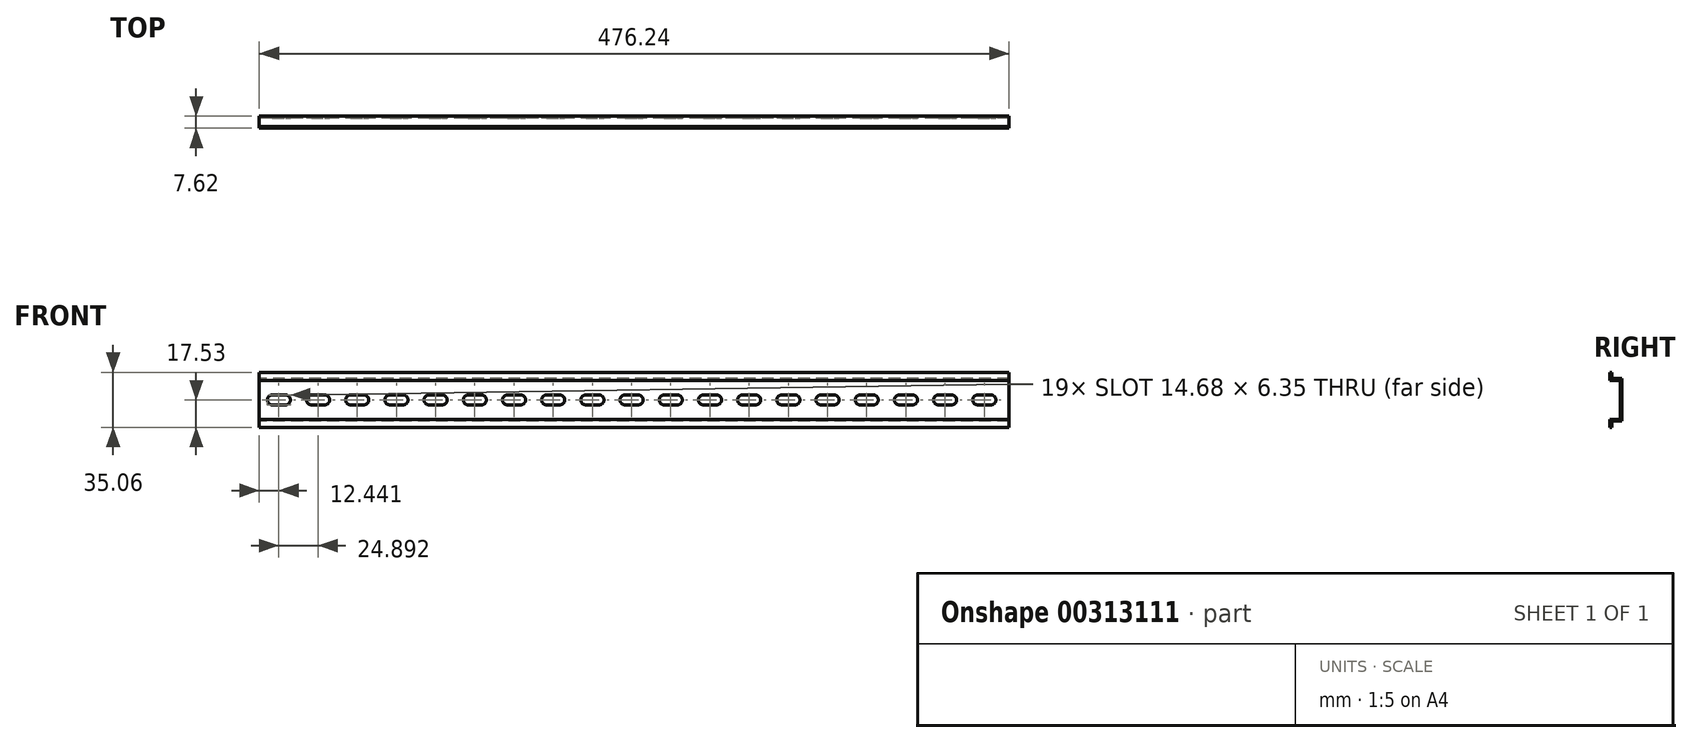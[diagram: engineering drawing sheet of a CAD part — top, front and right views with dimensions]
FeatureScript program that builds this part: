
annotation { "Feature Type Name" : "Feature", "Feature Type Description" : "" }
export const myFeature = defineFeature(function(context is Context, id is Id, definition is map)
    precondition{}
    {
        {
            var Q0;
            Q0=qCreatedBy(makeId("Right.planeOp"),FACE);
            var sketch = newSketch(context, id + "F0", { "sketchPlane" : qUnion([Q0])});
            skLineSegment(sketch, "E0", {"start": v(0, 17.53) * mm, "end": v(0, 12.45) * mm});
            skLineSegment(sketch, "E1", {"start": v(0, 12.45) * mm, "end": v(6.6, 12.45) * mm});
            skLineSegment(sketch, "E2", {"start": v(6.6, 12.45) * mm, "end": v(6.6, -12.45) * mm});
            skLineSegment(sketch, "E3", {"start": v(6.6, -12.45) * mm, "end": v(0, -12.45) * mm});
            skLineSegment(sketch, "E4", {"start": v(0, -12.45) * mm, "end": v(0, -17.53) * mm});
            skLineSegment(sketch, "E5", {"start": v(0, -17.53) * mm, "end": v(1.02, -17.53) * mm});
            skLineSegment(sketch, "E6", {"start": v(1.02, -17.53) * mm, "end": v(1.02, -13.46) * mm});
            skLineSegment(sketch, "E7", {"start": v(1.02, -13.46) * mm, "end": v(7.62, -13.46) * mm});
            skLineSegment(sketch, "E8", {"start": v(7.62, -13.46) * mm, "end": v(7.62, 13.46) * mm});
            skLineSegment(sketch, "E9", {"start": v(7.62, 13.46) * mm, "end": v(1.02, 13.46) * mm});
            skLineSegment(sketch, "E10", {"start": v(1.02, 13.46) * mm, "end": v(1.02, 17.53) * mm});
            skLineSegment(sketch, "E11", {"start": v(1.02, 17.53) * mm, "end": v(0, 17.53) * mm});
            skPoint(sketch, "E12", {"position": v(6.6, 0) * mm});
            skSolve(sketch);
        }
        {
            var Q0;
            Q0 = qSketchRegion(id + "F0", true);
            extrude(context, id + "F1", {"entities" : qUnion([Q0]), "endBound" : BoundingType.SYMMETRIC, "depth" : 476.25 * mm});
        }
        {
            var Q0;
            Q0=makeQuery(id+"F1.opExtrude","SWEPT_FACE",FACE,{"disambiguationData":[OSD([sQuery(id+"F0.wireOp",EDGE,"E2")])]});
            var sketch = newSketch(context, id + "F2", { "sketchPlane" : qUnion([Q0])});
            skArc(sketch, "E13", {"start": v(-229.85, -3.18) * mm, "mid": v(-233.02, 0) * mm, "end": v(-229.85, 3.18) * mm});
            skPoint(sketch, "E13.centerSnap0", {"position": v(-238.13, 0) * mm});
            skArc(sketch, "E14", {"start": v(-221.51, 3.18) * mm, "mid": v(-218.34, 0) * mm, "end": v(-221.51, -3.17) * mm});
            skLineSegment(sketch, "E15", {"start": v(-229.85, 3.17) * mm, "end": v(-221.51, 3.17) * mm});
            skLineSegment(sketch, "E16", {"start": v(-229.85, -3.17) * mm, "end": v(-221.51, -3.17) * mm});
            skPoint(sketch, "E17", {"position": v(-225.68, 3.18) * mm});
            skPoint(sketch, "E18", {"position": v(-225.68, -3.18) * mm});
            skLineSegment(sketch, "E19", {"start": v(-225.68, 3.18) * mm, "end": v(-225.68, -3.18) * mm, "construction": true});
            skPoint(sketch, "E20", {"position": v(-225.68, 0) * mm});
            skLineSegment(sketch, "E21.1.0.0", {"start": v(-204.95, 3.17) * mm, "end": v(-196.62, 3.17) * mm});
            skArc(sketch, "E21.1.0.1", {"start": v(-196.62, 3.18) * mm, "mid": v(-193.45, 0) * mm, "end": v(-196.62, -3.17) * mm});
            skLineSegment(sketch, "E21.1.0.2", {"start": v(-204.95, -3.17) * mm, "end": v(-196.62, -3.17) * mm});
            skArc(sketch, "E21.1.0.3", {"start": v(-204.95, -3.18) * mm, "mid": v(-208.13, 0) * mm, "end": v(-204.95, 3.18) * mm});
            skPoint(sketch, "E21.1.0.4", {"position": v(-200.79, 0) * mm});
            skPoint(sketch, "E21.1.0.5", {"position": v(-200.79, -3.18) * mm});
            skPoint(sketch, "E21.1.0.6", {"position": v(-200.79, 3.18) * mm});
            skPoint(sketch, "E21.1.0.7", {"position": v(-213.23, 0) * mm});
            skLineSegment(sketch, "E21.1.0.8", {"start": v(-200.79, 3.18) * mm, "end": v(-200.79, -3.18) * mm, "construction": true});
            skLineSegment(sketch, "E21.2.0.0", {"start": v(-180.06, 3.17) * mm, "end": v(-171.73, 3.17) * mm});
            skArc(sketch, "E21.2.0.1", {"start": v(-171.73, 3.18) * mm, "mid": v(-168.55, 0) * mm, "end": v(-171.73, -3.17) * mm});
            skLineSegment(sketch, "E21.2.0.2", {"start": v(-180.06, -3.17) * mm, "end": v(-171.73, -3.17) * mm});
            skArc(sketch, "E21.2.0.3", {"start": v(-180.06, -3.18) * mm, "mid": v(-183.24, 0) * mm, "end": v(-180.06, 3.18) * mm});
            skPoint(sketch, "E21.2.0.4", {"position": v(-175.9, 0) * mm});
            skPoint(sketch, "E21.2.0.5", {"position": v(-175.9, -3.18) * mm});
            skPoint(sketch, "E21.2.0.6", {"position": v(-175.9, 3.18) * mm});
            skPoint(sketch, "E21.2.0.7", {"position": v(-188.34, 0) * mm});
            skLineSegment(sketch, "E21.2.0.8", {"start": v(-175.9, 3.18) * mm, "end": v(-175.9, -3.18) * mm, "construction": true});
            skLineSegment(sketch, "E21.3.0.0", {"start": v(-155.17, 3.17) * mm, "end": v(-146.84, 3.17) * mm});
            skArc(sketch, "E21.3.0.1", {"start": v(-146.84, 3.18) * mm, "mid": v(-143.66, 0) * mm, "end": v(-146.84, -3.17) * mm});
            skLineSegment(sketch, "E21.3.0.2", {"start": v(-155.17, -3.17) * mm, "end": v(-146.84, -3.17) * mm});
            skArc(sketch, "E21.3.0.3", {"start": v(-155.17, -3.18) * mm, "mid": v(-158.34, 0) * mm, "end": v(-155.17, 3.18) * mm});
            skPoint(sketch, "E21.3.0.4", {"position": v(-151, 0) * mm});
            skPoint(sketch, "E21.3.0.5", {"position": v(-151, -3.18) * mm});
            skPoint(sketch, "E21.3.0.6", {"position": v(-151, 3.18) * mm});
            skPoint(sketch, "E21.3.0.7", {"position": v(-163.45, 0) * mm});
            skLineSegment(sketch, "E21.3.0.8", {"start": v(-151, 3.18) * mm, "end": v(-151, -3.18) * mm, "construction": true});
            skLineSegment(sketch, "E21.4.0.0", {"start": v(-130.28, 3.17) * mm, "end": v(-121.94, 3.17) * mm});
            skArc(sketch, "E21.4.0.1", {"start": v(-121.94, 3.18) * mm, "mid": v(-118.77, 0) * mm, "end": v(-121.94, -3.17) * mm});
            skLineSegment(sketch, "E21.4.0.2", {"start": v(-130.28, -3.17) * mm, "end": v(-121.94, -3.17) * mm});
            skArc(sketch, "E21.4.0.3", {"start": v(-130.28, -3.18) * mm, "mid": v(-133.45, 0) * mm, "end": v(-130.28, 3.18) * mm});
            skPoint(sketch, "E21.4.0.4", {"position": v(-126.11, 0) * mm});
            skPoint(sketch, "E21.4.0.5", {"position": v(-126.11, -3.18) * mm});
            skPoint(sketch, "E21.4.0.6", {"position": v(-126.11, 3.18) * mm});
            skPoint(sketch, "E21.4.0.7", {"position": v(-138.56, 0) * mm});
            skLineSegment(sketch, "E21.4.0.8", {"start": v(-126.11, 3.18) * mm, "end": v(-126.11, -3.18) * mm, "construction": true});
            skLineSegment(sketch, "E21.5.0.0", {"start": v(-105.39, 3.17) * mm, "end": v(-97.05, 3.17) * mm});
            skArc(sketch, "E21.5.0.1", {"start": v(-97.05, 3.18) * mm, "mid": v(-93.88, 0) * mm, "end": v(-97.05, -3.17) * mm});
            skLineSegment(sketch, "E21.5.0.2", {"start": v(-105.39, -3.17) * mm, "end": v(-97.05, -3.17) * mm});
            skArc(sketch, "E21.5.0.3", {"start": v(-105.39, -3.18) * mm, "mid": v(-108.56, 0) * mm, "end": v(-105.39, 3.18) * mm});
            skPoint(sketch, "E21.5.0.4", {"position": v(-101.22, 0) * mm});
            skPoint(sketch, "E21.5.0.5", {"position": v(-101.22, -3.18) * mm});
            skPoint(sketch, "E21.5.0.6", {"position": v(-101.22, 3.18) * mm});
            skPoint(sketch, "E21.5.0.7", {"position": v(-113.67, 0) * mm});
            skLineSegment(sketch, "E21.5.0.8", {"start": v(-101.22, 3.18) * mm, "end": v(-101.22, -3.18) * mm, "construction": true});
            skLineSegment(sketch, "E21.6.0.0", {"start": v(-80.5, 3.17) * mm, "end": v(-72.16, 3.17) * mm});
            skArc(sketch, "E21.6.0.1", {"start": v(-72.16, 3.18) * mm, "mid": v(-68.99, 0) * mm, "end": v(-72.16, -3.17) * mm});
            skLineSegment(sketch, "E21.6.0.2", {"start": v(-80.5, -3.17) * mm, "end": v(-72.16, -3.17) * mm});
            skArc(sketch, "E21.6.0.3", {"start": v(-80.5, -3.18) * mm, "mid": v(-83.67, 0) * mm, "end": v(-80.5, 3.18) * mm});
            skPoint(sketch, "E21.6.0.4", {"position": v(-76.33, 0) * mm});
            skPoint(sketch, "E21.6.0.5", {"position": v(-76.33, -3.18) * mm});
            skPoint(sketch, "E21.6.0.6", {"position": v(-76.33, 3.18) * mm});
            skPoint(sketch, "E21.6.0.7", {"position": v(-88.77, 0) * mm});
            skLineSegment(sketch, "E21.6.0.8", {"start": v(-76.33, 3.18) * mm, "end": v(-76.33, -3.18) * mm, "construction": true});
            skLineSegment(sketch, "E21.7.0.0", {"start": v(-55.6, 3.17) * mm, "end": v(-47.27, 3.17) * mm});
            skArc(sketch, "E21.7.0.1", {"start": v(-47.27, 3.18) * mm, "mid": v(-44.1, 0) * mm, "end": v(-47.27, -3.17) * mm});
            skLineSegment(sketch, "E21.7.0.2", {"start": v(-55.6, -3.17) * mm, "end": v(-47.27, -3.17) * mm});
            skArc(sketch, "E21.7.0.3", {"start": v(-55.6, -3.18) * mm, "mid": v(-58.78, 0) * mm, "end": v(-55.6, 3.18) * mm});
            skPoint(sketch, "E21.7.0.4", {"position": v(-51.44, 0) * mm});
            skPoint(sketch, "E21.7.0.5", {"position": v(-51.43, -3.18) * mm});
            skPoint(sketch, "E21.7.0.6", {"position": v(-51.44, 3.18) * mm});
            skPoint(sketch, "E21.7.0.7", {"position": v(-63.88, 0) * mm});
            skLineSegment(sketch, "E21.7.0.8", {"start": v(-51.44, 3.18) * mm, "end": v(-51.43, -3.18) * mm, "construction": true});
            skLineSegment(sketch, "E21.8.0.0", {"start": v(-30.7, 3.17) * mm, "end": v(-22.38, 3.17) * mm});
            skArc(sketch, "E21.8.0.1", {"start": v(-22.38, 3.18) * mm, "mid": v(-19.2, 0) * mm, "end": v(-22.38, -3.17) * mm});
            skLineSegment(sketch, "E21.8.0.2", {"start": v(-30.7, -3.17) * mm, "end": v(-22.38, -3.17) * mm});
            skArc(sketch, "E21.8.0.3", {"start": v(-30.7, -3.18) * mm, "mid": v(-33.88, 0) * mm, "end": v(-30.7, 3.18) * mm});
            skPoint(sketch, "E21.8.0.4", {"position": v(-26.54, 0) * mm});
            skPoint(sketch, "E21.8.0.5", {"position": v(-26.54, -3.18) * mm});
            skPoint(sketch, "E21.8.0.6", {"position": v(-26.54, 3.18) * mm});
            skPoint(sketch, "E21.8.0.7", {"position": v(-38.99, 0) * mm});
            skLineSegment(sketch, "E21.8.0.8", {"start": v(-26.54, 3.18) * mm, "end": v(-26.54, -3.18) * mm, "construction": true});
            skLineSegment(sketch, "E21.9.0.0", {"start": v(-5.82, 3.17) * mm, "end": v(2.52, 3.17) * mm});
            skArc(sketch, "E21.9.0.1", {"start": v(2.52, 3.18) * mm, "mid": v(5.7, 0) * mm, "end": v(2.52, -3.17) * mm});
            skLineSegment(sketch, "E21.9.0.2", {"start": v(-5.82, -3.17) * mm, "end": v(2.52, -3.17) * mm});
            skArc(sketch, "E21.9.0.3", {"start": v(-5.82, -3.18) * mm, "mid": v(-9, 0) * mm, "end": v(-5.82, 3.18) * mm});
            skPoint(sketch, "E21.9.0.4", {"position": v(-1.65, 0) * mm});
            skPoint(sketch, "E21.9.0.5", {"position": v(-1.65, -3.18) * mm});
            skPoint(sketch, "E21.9.0.6", {"position": v(-1.65, 3.18) * mm});
            skPoint(sketch, "E21.9.0.7", {"position": v(-14.1, 0) * mm});
            skLineSegment(sketch, "E21.9.0.8", {"start": v(-1.65, 3.18) * mm, "end": v(-1.65, -3.18) * mm, "construction": true});
            skLineSegment(sketch, "E21.10.0.0", {"start": v(19.07, 3.17) * mm, "end": v(27.4, 3.17) * mm});
            skArc(sketch, "E21.10.0.1", {"start": v(27.4, 3.18) * mm, "mid": v(30.58, 0) * mm, "end": v(27.4, -3.17) * mm});
            skLineSegment(sketch, "E21.10.0.2", {"start": v(19.07, -3.17) * mm, "end": v(27.4, -3.17) * mm});
            skArc(sketch, "E21.10.0.3", {"start": v(19.07, -3.18) * mm, "mid": v(15.9, 0) * mm, "end": v(19.07, 3.18) * mm});
            skPoint(sketch, "E21.10.0.4", {"position": v(23.24, 0) * mm});
            skPoint(sketch, "E21.10.0.5", {"position": v(23.24, -3.18) * mm});
            skPoint(sketch, "E21.10.0.6", {"position": v(23.24, 3.18) * mm});
            skPoint(sketch, "E21.10.0.7", {"position": v(10.8, 0) * mm});
            skLineSegment(sketch, "E21.10.0.8", {"start": v(23.24, 3.18) * mm, "end": v(23.24, -3.18) * mm, "construction": true});
            skLineSegment(sketch, "E21.11.0.0", {"start": v(43.97, 3.17) * mm, "end": v(52.3, 3.17) * mm});
            skArc(sketch, "E21.11.0.1", {"start": v(52.3, 3.18) * mm, "mid": v(55.47, 0) * mm, "end": v(52.3, -3.17) * mm});
            skLineSegment(sketch, "E21.11.0.2", {"start": v(43.97, -3.17) * mm, "end": v(52.3, -3.17) * mm});
            skArc(sketch, "E21.11.0.3", {"start": v(43.97, -3.18) * mm, "mid": v(40.8, 0) * mm, "end": v(43.97, 3.18) * mm});
            skPoint(sketch, "E21.11.0.4", {"position": v(48.13, 0) * mm});
            skPoint(sketch, "E21.11.0.5", {"position": v(48.13, -3.18) * mm});
            skPoint(sketch, "E21.11.0.6", {"position": v(48.13, 3.18) * mm});
            skPoint(sketch, "E21.11.0.7", {"position": v(35.69, 0) * mm});
            skLineSegment(sketch, "E21.11.0.8", {"start": v(48.13, 3.18) * mm, "end": v(48.13, -3.18) * mm, "construction": true});
            skLineSegment(sketch, "E21.12.0.0", {"start": v(68.86, 3.17) * mm, "end": v(77.2, 3.17) * mm});
            skArc(sketch, "E21.12.0.1", {"start": v(77.2, 3.18) * mm, "mid": v(80.37, 0) * mm, "end": v(77.2, -3.17) * mm});
            skLineSegment(sketch, "E21.12.0.2", {"start": v(68.86, -3.17) * mm, "end": v(77.2, -3.17) * mm});
            skArc(sketch, "E21.12.0.3", {"start": v(68.86, -3.18) * mm, "mid": v(65.68, 0) * mm, "end": v(68.86, 3.18) * mm});
            skPoint(sketch, "E21.12.0.4", {"position": v(73.02, 0) * mm});
            skPoint(sketch, "E21.12.0.5", {"position": v(73.03, -3.18) * mm});
            skPoint(sketch, "E21.12.0.6", {"position": v(73.02, 3.18) * mm});
            skPoint(sketch, "E21.12.0.7", {"position": v(60.58, 0) * mm});
            skLineSegment(sketch, "E21.12.0.8", {"start": v(73.02, 3.18) * mm, "end": v(73.03, -3.18) * mm, "construction": true});
            skLineSegment(sketch, "E21.13.0.0", {"start": v(93.75, 3.17) * mm, "end": v(102.08, 3.17) * mm});
            skArc(sketch, "E21.13.0.1", {"start": v(102.08, 3.18) * mm, "mid": v(105.26, 0) * mm, "end": v(102.08, -3.17) * mm});
            skLineSegment(sketch, "E21.13.0.2", {"start": v(93.75, -3.17) * mm, "end": v(102.08, -3.17) * mm});
            skArc(sketch, "E21.13.0.3", {"start": v(93.75, -3.18) * mm, "mid": v(90.58, 0) * mm, "end": v(93.75, 3.18) * mm});
            skPoint(sketch, "E21.13.0.4", {"position": v(97.92, 0) * mm});
            skPoint(sketch, "E21.13.0.5", {"position": v(97.92, -3.18) * mm});
            skPoint(sketch, "E21.13.0.6", {"position": v(97.92, 3.18) * mm});
            skPoint(sketch, "E21.13.0.7", {"position": v(85.47, 0) * mm});
            skLineSegment(sketch, "E21.13.0.8", {"start": v(97.92, 3.18) * mm, "end": v(97.92, -3.18) * mm, "construction": true});
            skLineSegment(sketch, "E21.direction1", {"start": v(-238.13, 0) * mm, "end": v(-213.23, 0) * mm, "construction": true});
            skLineSegment(sketch, "E22.0.14.0", {"start": v(118.64, 3.17) * mm, "end": v(126.98, 3.17) * mm});
            skArc(sketch, "E22.3.14.0", {"start": v(126.98, 3.18) * mm, "mid": v(130.15, 0) * mm, "end": v(126.98, -3.17) * mm});
            skLineSegment(sketch, "E22.7.14.0", {"start": v(118.64, -3.17) * mm, "end": v(126.98, -3.17) * mm});
            skArc(sketch, "E22.10.14.0", {"start": v(118.64, -3.18) * mm, "mid": v(115.47, 0) * mm, "end": v(118.64, 3.18) * mm});
            skPoint(sketch, "E22.14.14.0", {"position": v(122.8, 0) * mm});
            skPoint(sketch, "E22.15.14.0", {"position": v(122.8, -3.18) * mm});
            skPoint(sketch, "E22.16.14.0", {"position": v(122.8, 3.18) * mm});
            skPoint(sketch, "E22.17.14.0", {"position": v(110.36, 0) * mm});
            skLineSegment(sketch, "E22.18.14.0", {"start": v(122.8, 3.18) * mm, "end": v(122.8, -3.18) * mm, "construction": true});
            skLineSegment(sketch, "E23.0.15.0", {"start": v(143.53, 3.17) * mm, "end": v(151.87, 3.17) * mm});
            skArc(sketch, "E23.3.15.0", {"start": v(151.87, 3.18) * mm, "mid": v(155.04, 0) * mm, "end": v(151.87, -3.17) * mm});
            skLineSegment(sketch, "E23.7.15.0", {"start": v(143.53, -3.17) * mm, "end": v(151.87, -3.17) * mm});
            skArc(sketch, "E23.10.15.0", {"start": v(143.53, -3.18) * mm, "mid": v(140.36, 0) * mm, "end": v(143.53, 3.18) * mm});
            skPoint(sketch, "E23.14.15.0", {"position": v(147.7, 0) * mm});
            skPoint(sketch, "E23.15.15.0", {"position": v(147.7, -3.18) * mm});
            skPoint(sketch, "E23.16.15.0", {"position": v(147.7, 3.18) * mm});
            skPoint(sketch, "E23.17.15.0", {"position": v(135.25, 0) * mm});
            skLineSegment(sketch, "E23.18.15.0", {"start": v(147.7, 3.18) * mm, "end": v(147.7, -3.18) * mm, "construction": true});
            skLineSegment(sketch, "E24.0.16.0", {"start": v(168.43, 3.17) * mm, "end": v(176.76, 3.17) * mm});
            skArc(sketch, "E24.3.16.0", {"start": v(176.76, 3.18) * mm, "mid": v(179.93, 0) * mm, "end": v(176.76, -3.17) * mm});
            skLineSegment(sketch, "E24.7.16.0", {"start": v(168.43, -3.17) * mm, "end": v(176.76, -3.17) * mm});
            skArc(sketch, "E24.10.16.0", {"start": v(168.43, -3.18) * mm, "mid": v(165.25, 0) * mm, "end": v(168.43, 3.18) * mm});
            skPoint(sketch, "E24.14.16.0", {"position": v(172.6, 0) * mm});
            skPoint(sketch, "E24.15.16.0", {"position": v(172.6, -3.18) * mm});
            skPoint(sketch, "E24.16.16.0", {"position": v(172.6, 3.18) * mm});
            skPoint(sketch, "E24.17.16.0", {"position": v(160.15, 0) * mm});
            skLineSegment(sketch, "E24.18.16.0", {"start": v(172.6, 3.18) * mm, "end": v(172.6, -3.18) * mm, "construction": true});
            skLineSegment(sketch, "E24.0.17.0", {"start": v(193.32, 3.17) * mm, "end": v(201.65, 3.17) * mm});
            skArc(sketch, "E24.3.17.0", {"start": v(201.65, 3.18) * mm, "mid": v(204.83, 0) * mm, "end": v(201.65, -3.17) * mm});
            skLineSegment(sketch, "E24.7.17.0", {"start": v(193.32, -3.17) * mm, "end": v(201.65, -3.17) * mm});
            skArc(sketch, "E24.10.17.0", {"start": v(193.32, -3.18) * mm, "mid": v(190.14, 0) * mm, "end": v(193.32, 3.18) * mm});
            skPoint(sketch, "E24.14.17.0", {"position": v(197.48, 0) * mm});
            skPoint(sketch, "E24.15.17.0", {"position": v(197.49, -3.18) * mm});
            skPoint(sketch, "E24.16.17.0", {"position": v(197.48, 3.18) * mm});
            skPoint(sketch, "E24.17.17.0", {"position": v(185.04, 0) * mm});
            skLineSegment(sketch, "E24.18.17.0", {"start": v(197.48, 3.18) * mm, "end": v(197.49, -3.18) * mm, "construction": true});
            skLineSegment(sketch, "E24.0.18.0", {"start": v(218.21, 3.17) * mm, "end": v(226.54, 3.17) * mm});
            skArc(sketch, "E24.3.18.0", {"start": v(226.54, 3.18) * mm, "mid": v(229.72, 0) * mm, "end": v(226.54, -3.17) * mm});
            skLineSegment(sketch, "E24.7.18.0", {"start": v(218.21, -3.17) * mm, "end": v(226.54, -3.17) * mm});
            skArc(sketch, "E24.10.18.0", {"start": v(218.21, -3.18) * mm, "mid": v(215.04, 0) * mm, "end": v(218.21, 3.18) * mm});
            skPoint(sketch, "E24.14.18.0", {"position": v(222.38, 0) * mm});
            skPoint(sketch, "E24.15.18.0", {"position": v(222.38, -3.18) * mm});
            skPoint(sketch, "E24.16.18.0", {"position": v(222.38, 3.18) * mm});
            skPoint(sketch, "E24.17.18.0", {"position": v(209.93, 0) * mm});
            skLineSegment(sketch, "E24.18.18.0", {"start": v(222.38, 3.18) * mm, "end": v(222.38, -3.18) * mm, "construction": true});
            skLineSegment(sketch, "E24.0.19.0", {"start": v(243.1, 3.17) * mm, "end": v(251.44, 3.17) * mm});
            skArc(sketch, "E24.3.19.0", {"start": v(251.44, 3.18) * mm, "mid": v(254.61, 0) * mm, "end": v(251.44, -3.17) * mm});
            skLineSegment(sketch, "E24.7.19.0", {"start": v(243.1, -3.17) * mm, "end": v(251.44, -3.17) * mm});
            skArc(sketch, "E24.10.19.0", {"start": v(243.1, -3.18) * mm, "mid": v(239.93, 0) * mm, "end": v(243.1, 3.18) * mm});
            skPoint(sketch, "E24.14.19.0", {"position": v(247.27, 0) * mm});
            skPoint(sketch, "E24.15.19.0", {"position": v(247.27, -3.18) * mm});
            skPoint(sketch, "E24.16.19.0", {"position": v(247.27, 3.18) * mm});
            skPoint(sketch, "E24.17.19.0", {"position": v(234.82, 0) * mm});
            skLineSegment(sketch, "E24.18.19.0", {"start": v(247.27, 3.18) * mm, "end": v(247.27, -3.18) * mm, "construction": true});
            skSolve(sketch);
        }
        {
            var Q0;
            Q0=makeQuery(id+"F2.imprint","IMPRINT",FACE,{"disambiguationData":[TD([[makeQuery(id+"F2.imprint","IMPRINT",EDGE,{"derivedFrom":sQuery(id+"F2.wireOp",EDGE,"E21.1.0.0")}),-1.0]])]});
            var Q1;
            Q1 = qSketchRegion(id + "F2", true);
            extrude(context, id + "F3", {"entities" : qUnion([Q0, Q1]), "operationType" : NewBodyOperationType.REMOVE, "endBound" : BoundingType.THROUGH_ALL, "oppositeDirection" : true, "depth" : 25.4 * mm});
        }
    });
